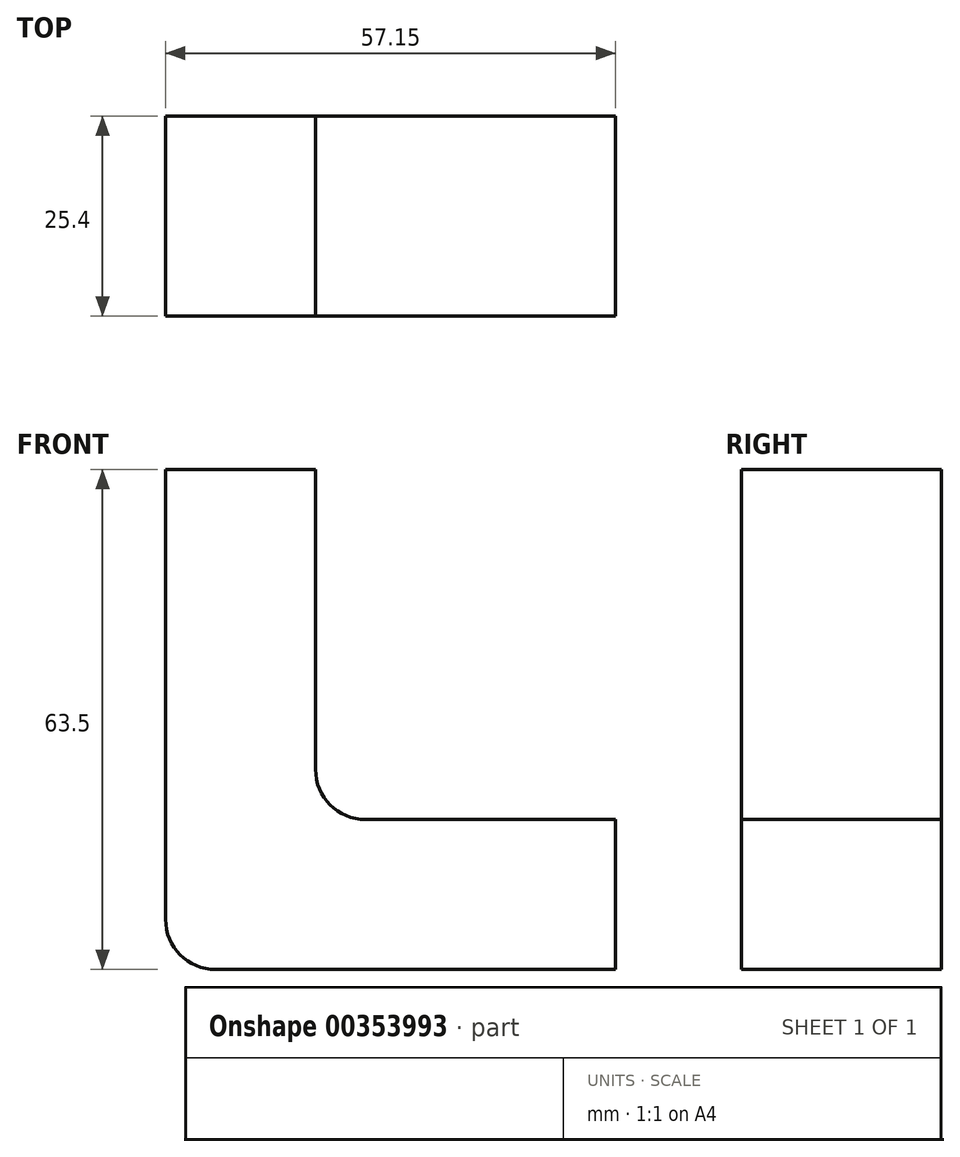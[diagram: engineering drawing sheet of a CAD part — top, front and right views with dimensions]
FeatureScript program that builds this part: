
annotation { "Feature Type Name" : "Feature", "Feature Type Description" : "" }
export const myFeature = defineFeature(function(context is Context, id is Id, definition is map)
    precondition{}
    {
        {
            var Q0;
            Q0=qCreatedBy(makeId("Front.planeOp"),FACE);
            var sketch = newSketch(context, id + "F0", { "sketchPlane" : qUnion([Q0])});
            skLineSegment(sketch, "E0", {"start": v(-25.1, 29.38) * mm, "end": v(-25.1, -27.77) * mm});
            skLineSegment(sketch, "E1", {"start": v(-18.74, -34.12) * mm, "end": v(32.06, -34.12) * mm});
            skLineSegment(sketch, "E2", {"start": v(-25.1, 29.38) * mm, "end": v(-6.04, 29.38) * mm});
            skLineSegment(sketch, "E3", {"start": v(-6.04, 29.38) * mm, "end": v(-6.04, -8.72) * mm});
            skLineSegment(sketch, "E4", {"start": v(0.3, -15.07) * mm, "end": v(32.06, -15.07) * mm});
            skLineSegment(sketch, "E5", {"start": v(32.06, -34.12) * mm, "end": v(32.06, -15.07) * mm});
            skArc(sketch, "E6.filletArc", {"start": v(-25.1, -27.77) * mm, "mid": v(-23.23, -32.26) * mm, "end": v(-18.74, -34.12) * mm});
            skPoint(sketch, "E7.visualSharp", {"position": v(-6.04, -15.07) * mm});
            skArc(sketch, "E7.filletArc", {"start": v(-6.04, -8.72) * mm, "mid": v(-4.18, -13.21) * mm, "end": v(0.3, -15.07) * mm});
            skSolve(sketch);
        }
        {
            var Q0;
            Q0=makeQuery(id+"F0.imprint","IMPRINT",FACE,{"disambiguationData":[TD([[makeQuery(id+"F0.imprint","IMPRINT",EDGE,{"derivedFrom":sQuery(id+"F0.wireOp",EDGE,"E0")}),1.0]])]});
            extrude(context, id + "F1", {"entities" : qUnion([Q0]), "depth" : 25.4 * mm});
        }
    });
